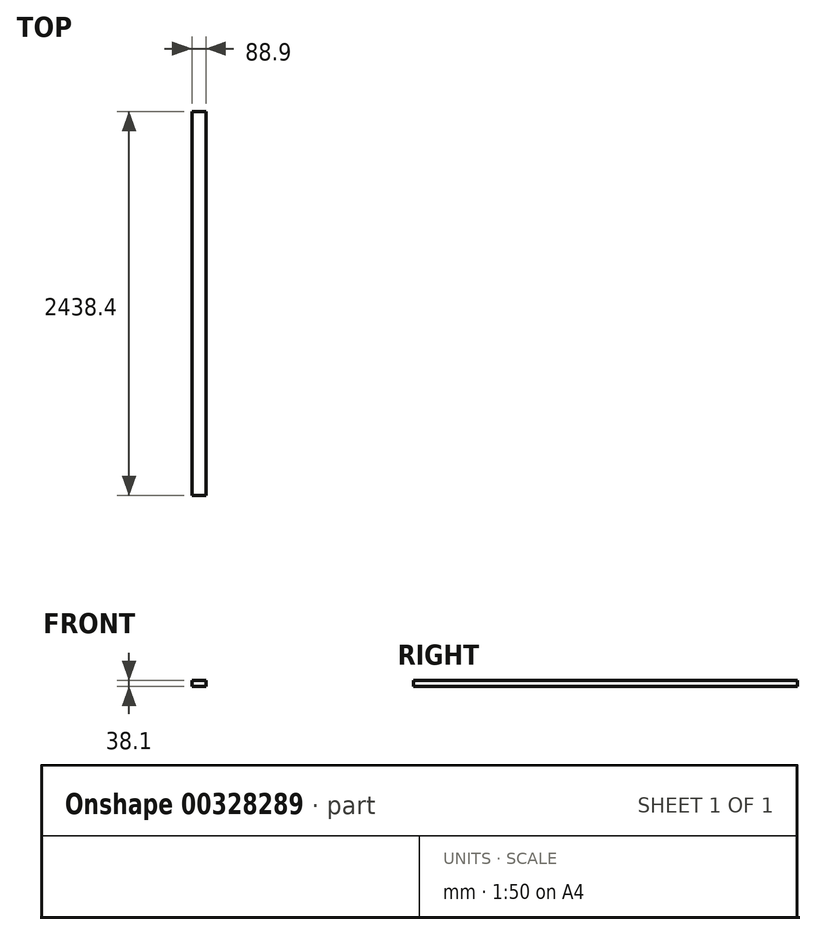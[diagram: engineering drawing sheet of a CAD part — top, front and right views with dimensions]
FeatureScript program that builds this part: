
annotation { "Feature Type Name" : "Feature", "Feature Type Description" : "" }
export const myFeature = defineFeature(function(context is Context, id is Id, definition is map)
    precondition{}
    {
        {
            var Q0;
            Q0=qCreatedBy(makeId("Front.planeOp"),FACE);
            var sketch = newSketch(context, id + "F0", { "sketchPlane" : qUnion([Q0])});
            skLineSegment(sketch, "E0.bottom", {"start": v(44.45, 19.05) * mm, "end": v(-44.45, 19.05) * mm});
            skLineSegment(sketch, "E0.top", {"start": v(44.45, -19.05) * mm, "end": v(-44.45, -19.05) * mm});
            skLineSegment(sketch, "E0.left", {"start": v(44.45, 19.05) * mm, "end": v(44.45, -19.05) * mm});
            skLineSegment(sketch, "E0.right", {"start": v(-44.45, 19.05) * mm, "end": v(-44.45, -19.05) * mm});
            skPoint(sketch, "E0.middle", {"position": v(0, 0) * mm});
            skSolve(sketch);
        }
        {
            var Q0;
            Q0=makeQuery(id+"F0.imprint","IMPRINT",FACE,{"disambiguationData":[TD([[makeQuery(id+"F0.imprint","IMPRINT",EDGE,{"derivedFrom":sQuery(id+"F0.wireOp",EDGE,"E0.bottom")}),1.0]])]});
            extrude(context, id + "F1", {"entities" : qUnion([Q0]), "depth" : 1219.2 * mm, "hasSecondDirection" : true, "secondDirectionOppositeDirection" : true, "secondDirectionDepth" : 1219.2 * mm});
        }
    });
